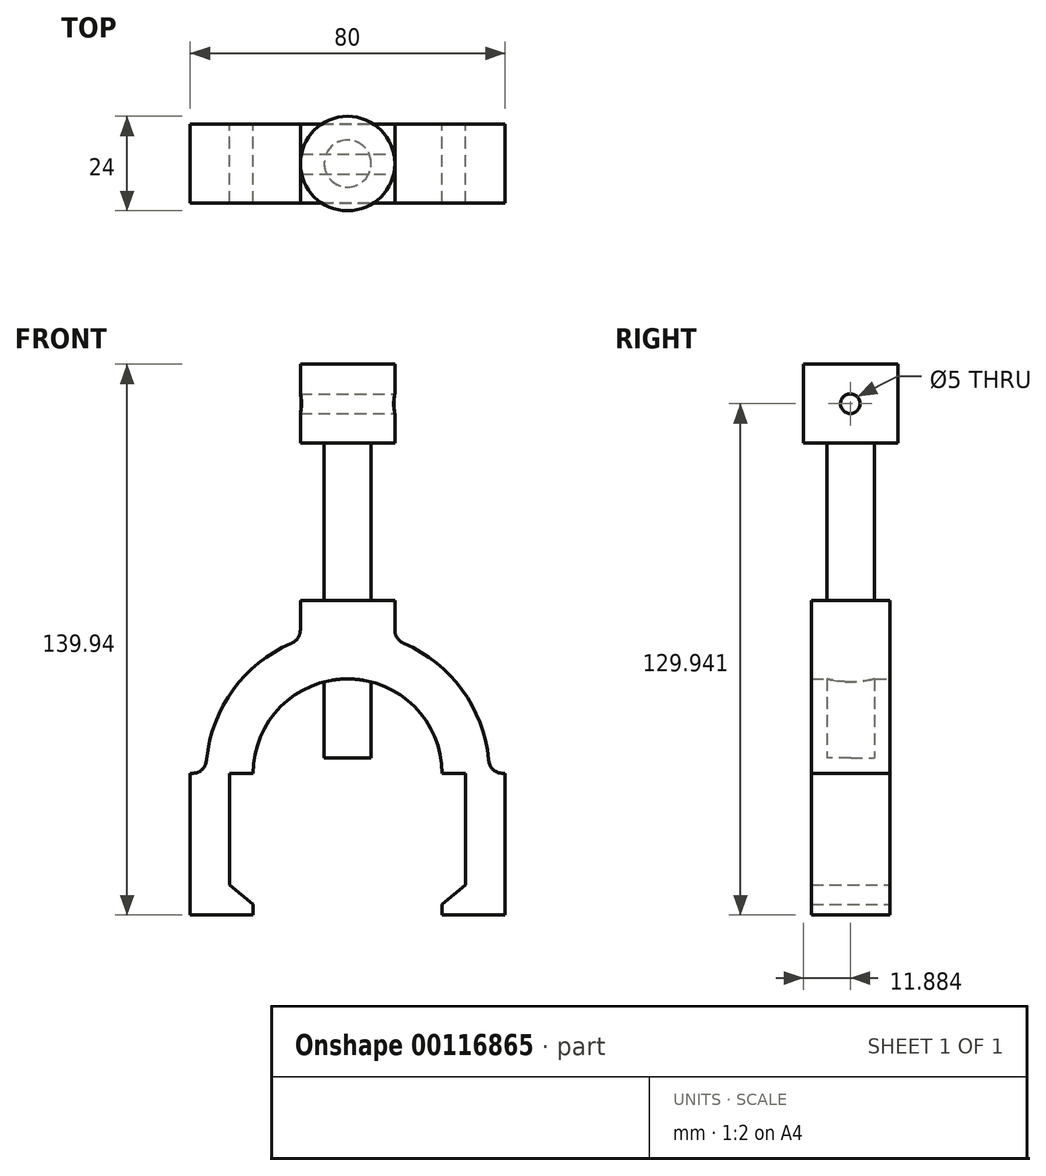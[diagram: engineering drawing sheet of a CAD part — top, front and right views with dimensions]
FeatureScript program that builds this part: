
annotation { "Feature Type Name" : "Feature", "Feature Type Description" : "" }
export const myFeature = defineFeature(function(context is Context, id is Id, definition is map)
    precondition{}
    {
        {
            var Q0;
            Q0=qCreatedBy(makeId("Front.planeOp"),FACE);
            var sketch = newSketch(context, id + "F0", { "sketchPlane" : qUnion([Q0])});
            skLineSegment(sketch, "E0", {"start": v(-36, 0) * mm, "end": v(36, 0) * mm});
            skPoint(sketch, "E1", {"position": v(0, 0) * mm});
            skArc(sketch, "E2", {"start": v(36, 0) * mm, "mid": v(29.4, 20.78) * mm, "end": v(12, 33.94) * mm});
            skArc(sketch, "E3", {"start": v(24, 0) * mm, "mid": v(0, 24) * mm, "end": v(-24, 0) * mm});
            skLineSegment(sketch, "E4", {"start": v(0, -15.48) * mm, "end": v(0, 54.13) * mm, "construction": true});
            skPoint(sketch, "E5", {"position": v(0, 39.94) * mm});
            skLineSegment(sketch, "E6", {"start": v(-12, 43.94) * mm, "end": v(12, 43.94) * mm});
            skPoint(sketch, "E7", {"position": v(0, 43.94) * mm});
            skLineSegment(sketch, "E8", {"start": v(-12, 43.94) * mm, "end": v(-12, 33.94) * mm});
            skLineSegment(sketch, "E9", {"start": v(12, 43.94) * mm, "end": v(12, 33.94) * mm});
            skArc(sketch, "E10.trimOffspring", {"start": v(-12, 33.94) * mm, "mid": v(-29.4, 20.78) * mm, "end": v(-36, 0) * mm});
            skLineSegment(sketch, "E11", {"start": v(30, 0) * mm, "end": v(30, -28.37) * mm});
            skLineSegment(sketch, "E12", {"start": v(36, 0) * mm, "end": v(40, 0) * mm});
            skLineSegment(sketch, "E13", {"start": v(40, 0) * mm, "end": v(40, -28.37) * mm});
            skLineSegment(sketch, "E14", {"start": v(30, -28.37) * mm, "end": v(24, -33.25) * mm});
            skLineSegment(sketch, "E15", {"start": v(24, -33.25) * mm, "end": v(24, -36) * mm});
            skLineSegment(sketch, "E16", {"start": v(24, -36) * mm, "end": v(40, -36) * mm});
            skLineSegment(sketch, "E17", {"start": v(40, -36) * mm, "end": v(40, -28.37) * mm});
            skLineSegment(sketch, "E18.MirrorCS", {"start": v(-30, 0) * mm, "end": v(-30, -28.37) * mm});
            skLineSegment(sketch, "E19.MirrorCS", {"start": v(-30, -28.37) * mm, "end": v(-24, -33.25) * mm});
            skLineSegment(sketch, "E20.MirrorCS", {"start": v(-24, -33.25) * mm, "end": v(-24, -36) * mm});
            skLineSegment(sketch, "E21.MirrorCS", {"start": v(-24, -36) * mm, "end": v(-40, -36) * mm});
            skLineSegment(sketch, "E22.MirrorCS", {"start": v(-40, -36) * mm, "end": v(-40, -28.37) * mm});
            skLineSegment(sketch, "E23", {"start": v(-36, 0) * mm, "end": v(-40, 0) * mm});
            skLineSegment(sketch, "E24", {"start": v(-40, 0) * mm, "end": v(-40, -28.37) * mm});
            skSolve(sketch);
        }
        {
            var Q0;
            {var subQ0=sQuery(id+"F0.wireOp",EDGE,"E2");Q0=makeQuery(id+"F0.imprint","IMPRINT",FACE,{"disambiguationData":[TD([[makeQuery(id+"F0.imprint","IMPRINT",EDGE,{"derivedFrom":subQ0}),1.0]])]});}
            var Q1;
            {var subQ1=sQuery(id+"F0.wireOp",EDGE,"4ec35f8d-0be9-4d28-b750-2281ee3214940.MirrorCS");Q1=makeQuery(id+"F0.imprint","IMPRINT",FACE,{"disambiguationData":[TD([[makeQuery(id+"F0.imprint","IMPRINT",EDGE,{"derivedFrom":subQ1}),1.0]])]});}
            var Q2;
            {var subQ0=sQuery(id+"F0.wireOp",EDGE,"0Nk4mLKa-v6s4-qZ9Q-IHuP-ThspCc0z5oUh");Q2=makeQuery(id+"F0.imprint","IMPRINT",FACE,{"disambiguationData":[TD([[makeQuery(id+"F0.imprint","IMPRINT",EDGE,{"derivedFrom":subQ0}),-1.0]])]});}
            var Q3;
            {var subQ2=sQuery(id+"F0.wireOp",EDGE,"E18.MirrorCS");Q3=makeQuery(id+"F0.imprint","IMPRINT",FACE,{"disambiguationData":[TD([[makeQuery(id+"F0.imprint","IMPRINT",EDGE,{"derivedFrom":subQ2}),-1.0]])]});}
            var Q4;
            {var subQ1=sQuery(id+"F0.wireOp",EDGE,"E11");Q4=makeQuery(id+"F0.imprint","IMPRINT",FACE,{"disambiguationData":[TD([[makeQuery(id+"F0.imprint","IMPRINT",EDGE,{"derivedFrom":subQ1}),1.0]])]});}
            extrude(context, id + "F1", {"entities" : qUnion([Q0, Q1, Q2, Q3, Q4]), "depth" : 20 * mm});
        }
        {
            var Q0;
            Q0=makeQuery(id+"F1.opExtrude","SWEPT_FACE",FACE,{"disambiguationData":[OSD([sQuery(id+"F0.wireOp",EDGE,"E6")])]});
            var sketch = newSketch(context, id + "F2", { "sketchPlane" : qUnion([Q0])});
            skLineSegment(sketch, "E25", {"start": v(-12, -10) * mm, "end": v(12, -10) * mm, "construction": true});
            skLineSegment(sketch, "E26", {"start": v(0, 0) * mm, "end": v(0, -20) * mm, "construction": true});
            skPoint(sketch, "E27", {"position": v(0, -10) * mm});
            skCircle(sketch, "E28", {"center": v(0, -10) * mm, "radius": 6 * mm});
            skSolve(sketch);
        }
        {
            var Q0;
            Q0=makeQuery(id+"F2.imprint","IMPRINT",FACE,{"disambiguationData":[TD([[makeQuery(id+"F2.imprint","IMPRINT",EDGE,{"derivedFrom":sQuery(id+"F2.wireOp",EDGE,"E28")}),1.0]])]});
            extrude(context, id + "F3", {"entities" : qUnion([Q0]), "operationType" : NewBodyOperationType.ADD, "depth" : 40 * mm, "hasSecondDirection" : true, "secondDirectionOppositeDirection" : true, "secondDirectionDepth" : 40 * mm});
        }
        {
            var Q0;
            Q0=makeQuery(id+"F3.opExtrude","CAP_FACE",FACE,{"disambiguationData":[OSD([sQuery(id+"F2.wireOp",EDGE,"E28")])],"isStart":false});
            var sketch = newSketch(context, id + "F4", { "sketchPlane" : qUnion([Q0])});
            skPoint(sketch, "E29", {"position": v(0, -10) * mm});
            skCircle(sketch, "E30", {"center": v(0, -10) * mm, "radius": 12 * mm});
            skSolve(sketch);
        }
        {
            var Q0;
            Q0 = qSketchRegion(id + "F4", true);
            extrude(context, id + "F5", {"entities" : qUnion([Q0]), "operationType" : NewBodyOperationType.ADD, "depth" : 20 * mm});
        }
        {
            var Q0;
            Q0=qCreatedBy(makeId("Right.planeOp"),FACE);
            cPlane(context, id + "F6", {"entities" : qUnion([Q0]), "cplaneType" : CPlaneType.OFFSET, "offset" : 12 * mm, "width" : 150 * mm, "height" : 150 * mm});
        }
        {
            var Q0;
            Q0=qCreatedBy(id+"F6.planeOp",FACE);
            var sketch = newSketch(context, id + "F7", { "sketchPlane" : qUnion([Q0])});
            skCircle(sketch, "E31", {"center": v(-10.12, 93.94) * mm, "radius": 2.5 * mm});
            skSolve(sketch);
        }
        {
            var Q0;
            Q0 = qSketchRegion(id + "F7", true);
            extrude(context, id + "F8", {"entities" : qUnion([Q0]), "operationType" : NewBodyOperationType.REMOVE, "oppositeDirection" : true, "depth" : 25 * mm});
        }
        {
            var Q0;
            Q0=makeQuery(id+"F1.opExtrude","SWEPT_EDGE",EDGE,{"disambiguationData":[OSD([sQuery(id+"F0.wireOp",EDGE,"E0"),sQuery(id+"F0.wireOp",EDGE,"E2"),sQuery(id+"F0.wireOp",EDGE,"E12")])]});
            var Q1;
            Q1=makeQuery(id+"F1.opExtrude","SWEPT_EDGE",EDGE,{"disambiguationData":[OSD([sQuery(id+"F0.wireOp",EDGE,"E0"),sQuery(id+"F0.wireOp",EDGE,"E10.trimOffspring"),sQuery(id+"F0.wireOp",EDGE,"E23")])]});
            var Q2;
            Q2=makeQuery(id+"F1.opExtrude","SWEPT_EDGE",EDGE,{"disambiguationData":[OSD([sQuery(id+"F0.wireOp",EDGE,"E8"),sQuery(id+"F0.wireOp",EDGE,"E10.trimOffspring")])]});
            var Q3;
            Q3=makeQuery(id+"F1.opExtrude","SWEPT_EDGE",EDGE,{"disambiguationData":[OSD([sQuery(id+"F0.wireOp",EDGE,"E2"),sQuery(id+"F0.wireOp",EDGE,"E9")])]});
            fillet(context, id + "F9", {"entities" : qUnion([Q0, Q1, Q2, Q3]), "radius" : 4 * mm, "tangentPropagation" : true, "rho" : 0.5, "crossSection" : FilletCrossSection.CONIC, "allowEdgeOverflow" : false});
        }
    });
